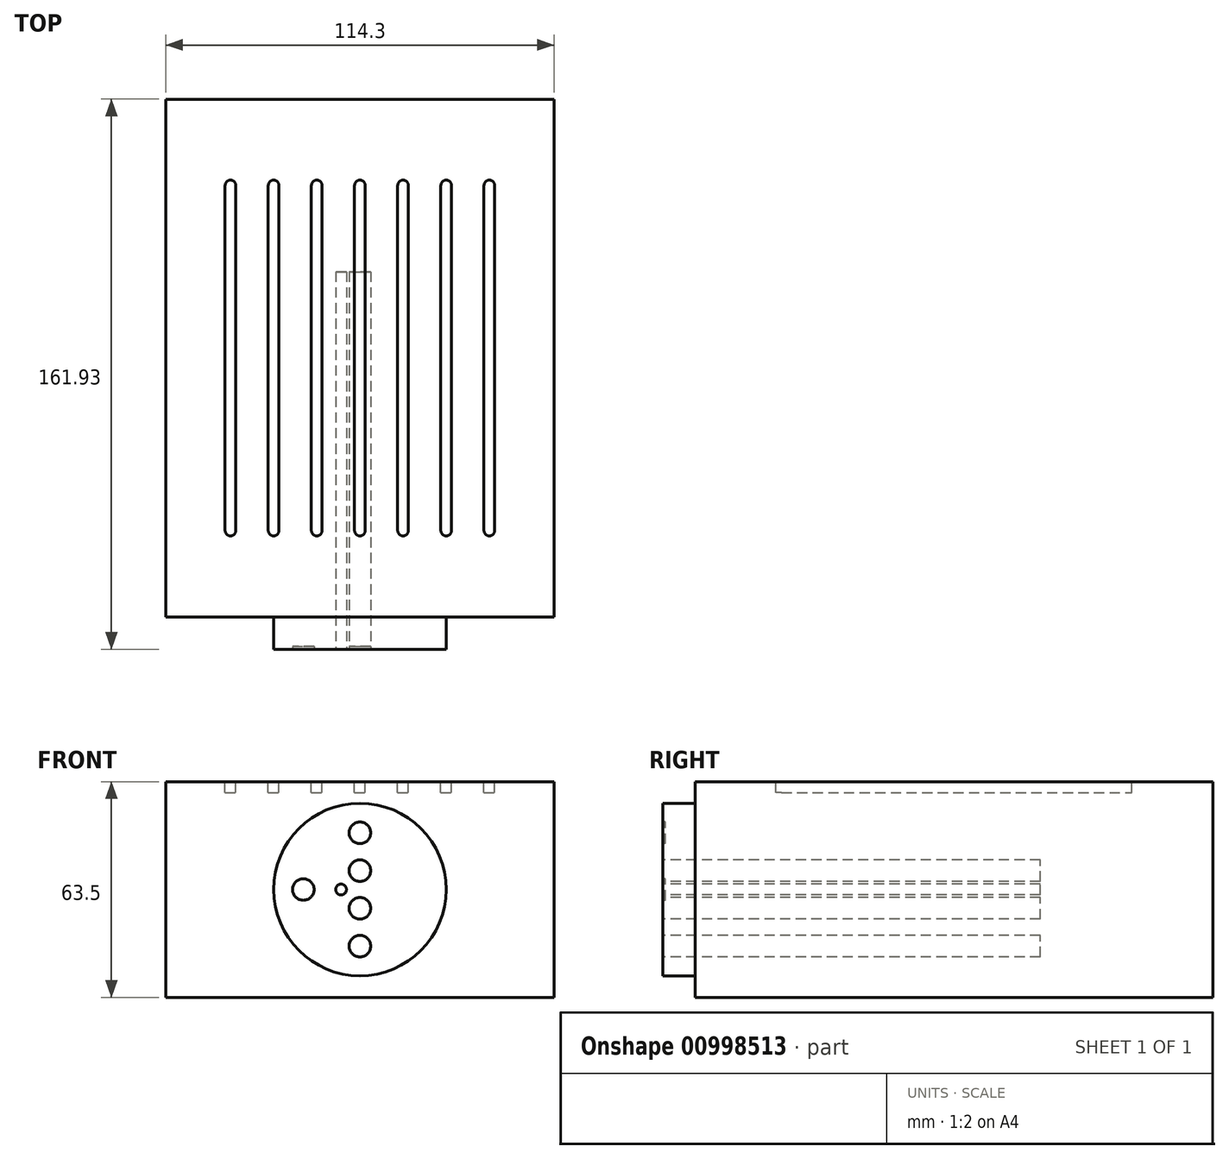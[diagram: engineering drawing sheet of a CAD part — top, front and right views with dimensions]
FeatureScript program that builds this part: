
annotation { "Feature Type Name" : "Feature", "Feature Type Description" : "" }
export const myFeature = defineFeature(function(context is Context, id is Id, definition is map)
    precondition{}
    {
        {
            var Q0;
            Q0=qCreatedBy(makeId("Front.planeOp"),FACE);
            var sketch = newSketch(context, id + "F0", { "sketchPlane" : qUnion([Q0])});
            skCircle(sketch, "E0", {"center": v(0, 0) * mm, "radius": 25.4 * mm});
            skLineSegment(sketch, "E1", {"start": v(0, 0) * mm, "end": v(0, -22.23) * mm, "construction": true});
            skCircle(sketch, "E2", {"center": v(0, -11.11) * mm, "radius": 11.11 * mm, "construction": true});
            skLineSegment(sketch, "E3", {"start": v(0, 0) * mm, "end": v(0, -11.11) * mm, "construction": true});
            skLineSegment(sketch, "E4", {"start": v(0, -11.11) * mm, "end": v(0, -22.23) * mm, "construction": true});
            skCircle(sketch, "E5", {"center": v(0, -5.56) * mm, "radius": 3.18 * mm});
            skCircle(sketch, "E6", {"center": v(0, -16.67) * mm, "radius": 3.18 * mm});
            skCircle(sketch, "E7.1.0", {"center": v(0, 5.56) * mm, "radius": 3.18 * mm});
            skCircle(sketch, "E7.1.1", {"center": v(0, 16.67) * mm, "radius": 3.18 * mm});
            skCircle(sketch, "E8", {"center": v(-16.67, 0) * mm, "radius": 3.18 * mm});
            skCircle(sketch, "E9", {"center": v(-5.56, 0) * mm, "radius": 1.59 * mm});
            skSolve(sketch);
        }
        {
            var Q0;
            Q0=makeQuery(id+"F0.imprint","IMPRINT",FACE,{"disambiguationData":[TD([[makeQuery(id+"F0.imprint","IMPRINT",EDGE,{"derivedFrom":sQuery(id+"F0.wireOp",EDGE,"E0")}),1.0]])]});
            var Q1;
            Q1=makeQuery(id+"F0.imprint","IMPRINT",FACE,{"disambiguationData":[TD([[makeQuery(id+"F0.imprint","IMPRINT",EDGE,{"derivedFrom":sQuery(id+"F0.wireOp",EDGE,"E8")}),1.0]])]});
            var Q2;
            Q2=makeQuery(id+"F0.imprint","IMPRINT",FACE,{"disambiguationData":[TD([[makeQuery(id+"F0.imprint","IMPRINT",EDGE,{"derivedFrom":sQuery(id+"F0.wireOp",EDGE,"E7.1.1")}),1.0]])]});
            extrude(context, id + "F1", {"entities" : qUnion([Q0, Q1, Q2]), "oppositeDirection" : true, "depth" : 9.52 * mm, "offsetDistance" : 25.4 * mm});
        }
        {
            var Q0;
            Q0=makeQuery(id+"F1.opExtrude","CAP_FACE",FACE,{"disambiguationData":[OSD([sQuery(id+"F0.wireOp",EDGE,"bLrKrRyo-NOmt-zjUR-0U13-k7j1eWPFAlHC"),sQuery(id+"F0.wireOp",EDGE,"oxDvdeo9-2tOV-YATh-vV8f-WV8PJaf9Di6w"),sQuery(id+"F0.wireOp",EDGE,"E0")])],"isStart":false});
            var sketch = newSketch(context, id + "F2", { "sketchPlane" : qUnion([Q0])});
            skLineSegment(sketch, "E10.bottom", {"start": v(57.15, 31.75) * mm, "end": v(-57.15, 31.75) * mm});
            skLineSegment(sketch, "E10.top", {"start": v(57.15, -31.75) * mm, "end": v(-57.15, -31.75) * mm});
            skLineSegment(sketch, "E10.left", {"start": v(57.15, 31.75) * mm, "end": v(57.15, -31.75) * mm});
            skLineSegment(sketch, "E10.right", {"start": v(-57.15, 31.75) * mm, "end": v(-57.15, -31.75) * mm});
            skPoint(sketch, "E10.middle", {"position": v(0, 0) * mm});
            skSolve(sketch);
        }
        {
            var Q0;
            Q0 = qSketchRegion(id + "F2", true);
            extrude(context, id + "F3", {"entities" : qUnion([Q0]), "operationType" : NewBodyOperationType.ADD, "depth" : 152.4 * mm, "offsetDistance" : 25.4 * mm});
        }
        {
            var Q0;
            Q0=makeQuery(id+"F3.opExtrude","SWEPT_FACE",FACE,{"disambiguationData":[OSD([sQuery(id+"F2.wireOp",EDGE,"E10.bottom")])]});
            var sketch = newSketch(context, id + "F4", { "sketchPlane" : qUnion([Q0])});
            skLineSegment(sketch, "E11", {"start": v(0, 34.93) * mm, "end": v(0, 136.53) * mm, "construction": true});
            skPoint(sketch, "E11.startSnap0", {"position": v(0, 9.53) * mm});
            skPoint(sketch, "E11.endSnap0", {"position": v(0, 161.93) * mm});
            skArc(sketch, "E12.0.startCap", {"start": v(1.59, 34.93) * mm, "mid": v(0, 33.34) * mm, "end": v(-1.59, 34.93) * mm});
            skArc(sketch, "E12.0.endCap", {"start": v(-1.59, 136.53) * mm, "mid": v(0, 138.11) * mm, "end": v(1.59, 136.53) * mm});
            skLineSegment(sketch, "E12.0.left", {"start": v(-1.59, 34.93) * mm, "end": v(-1.59, 136.53) * mm});
            skLineSegment(sketch, "E12.0.right", {"start": v(1.59, 34.93) * mm, "end": v(1.59, 136.53) * mm});
            skLineSegment(sketch, "E13.1.0.0", {"start": v(11.11, 34.93) * mm, "end": v(11.11, 136.53) * mm});
            skLineSegment(sketch, "E13.1.0.1", {"start": v(14.29, 34.93) * mm, "end": v(14.29, 136.53) * mm});
            skLineSegment(sketch, "E13.1.0.2", {"start": v(12.7, 34.93) * mm, "end": v(12.7, 136.53) * mm, "construction": true});
            skArc(sketch, "E13.1.0.3", {"start": v(14.29, 34.93) * mm, "mid": v(12.7, 33.34) * mm, "end": v(11.11, 34.93) * mm});
            skArc(sketch, "E13.1.0.4", {"start": v(11.11, 136.53) * mm, "mid": v(12.7, 138.11) * mm, "end": v(14.29, 136.53) * mm});
            skLineSegment(sketch, "E13.2.0.0", {"start": v(23.81, 34.93) * mm, "end": v(23.81, 136.53) * mm});
            skLineSegment(sketch, "E13.2.0.1", {"start": v(26.99, 34.93) * mm, "end": v(26.99, 136.53) * mm});
            skLineSegment(sketch, "E13.2.0.2", {"start": v(25.4, 34.93) * mm, "end": v(25.4, 136.53) * mm, "construction": true});
            skArc(sketch, "E13.2.0.3", {"start": v(26.99, 34.93) * mm, "mid": v(25.4, 33.34) * mm, "end": v(23.81, 34.93) * mm});
            skArc(sketch, "E13.2.0.4", {"start": v(23.81, 136.53) * mm, "mid": v(25.4, 138.11) * mm, "end": v(26.99, 136.53) * mm});
            skLineSegment(sketch, "E13.3.0.0", {"start": v(36.51, 34.93) * mm, "end": v(36.51, 136.53) * mm});
            skLineSegment(sketch, "E13.3.0.1", {"start": v(39.69, 34.93) * mm, "end": v(39.69, 136.53) * mm});
            skLineSegment(sketch, "E13.3.0.2", {"start": v(38.1, 34.93) * mm, "end": v(38.1, 136.53) * mm, "construction": true});
            skArc(sketch, "E13.3.0.3", {"start": v(39.69, 34.93) * mm, "mid": v(38.1, 33.34) * mm, "end": v(36.51, 34.93) * mm});
            skArc(sketch, "E13.3.0.4", {"start": v(36.51, 136.53) * mm, "mid": v(38.1, 138.11) * mm, "end": v(39.69, 136.53) * mm});
            skLineSegment(sketch, "E13.direction1", {"start": v(-1.59, 34.93) * mm, "end": v(11.11, 34.93) * mm, "construction": true});
            skArc(sketch, "E14.MirrorCS", {"start": v(-23.81, 136.53) * mm, "mid": v(-25.4, 138.11) * mm, "end": v(-26.99, 136.53) * mm});
            skArc(sketch, "E15.MirrorCS", {"start": v(-26.99, 34.93) * mm, "mid": v(-25.4, 33.34) * mm, "end": v(-23.81, 34.93) * mm});
            skArc(sketch, "E16.MirrorCS", {"start": v(-11.11, 136.53) * mm, "mid": v(-12.7, 138.11) * mm, "end": v(-14.29, 136.53) * mm});
            skArc(sketch, "E17.MirrorCS", {"start": v(-14.29, 34.93) * mm, "mid": v(-12.7, 33.34) * mm, "end": v(-11.11, 34.93) * mm});
            skArc(sketch, "E18.MirrorCS", {"start": v(-39.69, 34.93) * mm, "mid": v(-38.1, 33.34) * mm, "end": v(-36.51, 34.93) * mm});
            skArc(sketch, "E19.MirrorCS", {"start": v(-36.51, 136.53) * mm, "mid": v(-38.1, 138.11) * mm, "end": v(-39.69, 136.53) * mm});
            skLineSegment(sketch, "E20.MirrorCS", {"start": v(-38.1, 34.93) * mm, "end": v(-38.1, 136.53) * mm, "construction": true});
            skLineSegment(sketch, "E21.MirrorCS", {"start": v(-14.29, 34.93) * mm, "end": v(-14.29, 136.53) * mm});
            skLineSegment(sketch, "E22.MirrorCS", {"start": v(-11.11, 34.93) * mm, "end": v(-11.11, 136.53) * mm});
            skLineSegment(sketch, "E23.MirrorCS", {"start": v(-25.4, 34.93) * mm, "end": v(-25.4, 136.53) * mm, "construction": true});
            skLineSegment(sketch, "E24.MirrorCS", {"start": v(-26.99, 34.93) * mm, "end": v(-26.99, 136.53) * mm});
            skLineSegment(sketch, "E25.MirrorCS", {"start": v(-23.81, 34.93) * mm, "end": v(-23.81, 136.53) * mm});
            skLineSegment(sketch, "E26.MirrorCS", {"start": v(-39.69, 34.93) * mm, "end": v(-39.69, 136.53) * mm});
            skLineSegment(sketch, "E27.MirrorCS", {"start": v(-12.7, 34.93) * mm, "end": v(-12.7, 136.53) * mm, "construction": true});
            skLineSegment(sketch, "E28.MirrorCS", {"start": v(-36.51, 34.93) * mm, "end": v(-36.51, 136.53) * mm});
            skSolve(sketch);
        }
        {
            var Q0;
            Q0 = qSketchRegion(id + "F4", true);
            extrude(context, id + "F5", {"entities" : qUnion([Q0]), "operationType" : NewBodyOperationType.REMOVE, "oppositeDirection" : true, "depth" : 3.17 * mm, "offsetDistance" : 25.4 * mm});
        }
        {
            var Q0;
            Q0=makeQuery(id+"F0.imprint","IMPRINT",FACE,{"disambiguationData":[TD([[makeQuery(id+"F0.imprint","IMPRINT",EDGE,{"derivedFrom":sQuery(id+"F0.wireOp",EDGE,"E7.1.1")}),1.0]])]});
            var Q1;
            Q1=makeQuery(id+"F0.imprint","IMPRINT",FACE,{"disambiguationData":[TD([[makeQuery(id+"F0.imprint","IMPRINT",EDGE,{"derivedFrom":sQuery(id+"F0.wireOp",EDGE,"E8")}),1.0]])]});
            extrude(context, id + "F6", {"entities" : qUnion([Q0, Q1]), "operationType" : NewBodyOperationType.REMOVE, "oppositeDirection" : true, "depth" : 0.8 * mm, "offsetDistance" : 25.4 * mm});
        }
        {
            var Q0;
            Q0=makeQuery(id+"F3.boolean.opBoolean","SPLIT",FACE,{"disambiguationData":[TD([makeQuery(id+"F1.opExtrude","SWEPT_FACE",FACE,{"disambiguationData":[OSD([sQuery(id+"F0.wireOp",EDGE,"E7.1.0")])]})])],"derivedFrom":makeQuery(id+"F3.opExtrude","CAP_FACE",FACE,{"disambiguationData":[OSD([sQuery(id+"F2.wireOp",EDGE,"E10.bottom"),sQuery(id+"F2.wireOp",EDGE,"E10.top"),sQuery(id+"F2.wireOp",EDGE,"E10.left"),sQuery(id+"F2.wireOp",EDGE,"E10.right")])],"isStart":true})});
            var Q1;
            Q1=makeQuery(id+"F3.boolean.opBoolean","SPLIT",FACE,{"disambiguationData":[TD([makeQuery(id+"F1.opExtrude","SWEPT_FACE",FACE,{"disambiguationData":[OSD([sQuery(id+"F0.wireOp",EDGE,"E9")])]})])],"derivedFrom":makeQuery(id+"F3.opExtrude","CAP_FACE",FACE,{"disambiguationData":[OSD([sQuery(id+"F2.wireOp",EDGE,"E10.bottom"),sQuery(id+"F2.wireOp",EDGE,"E10.top"),sQuery(id+"F2.wireOp",EDGE,"E10.left"),sQuery(id+"F2.wireOp",EDGE,"E10.right")])],"isStart":true})});
            var Q2;
            Q2=makeQuery(id+"F3.boolean.opBoolean","SPLIT",FACE,{"disambiguationData":[TD([makeQuery(id+"F1.opExtrude","SWEPT_FACE",FACE,{"disambiguationData":[OSD([sQuery(id+"F0.wireOp",EDGE,"E5")])]})])],"derivedFrom":makeQuery(id+"F3.opExtrude","CAP_FACE",FACE,{"disambiguationData":[OSD([sQuery(id+"F2.wireOp",EDGE,"E10.bottom"),sQuery(id+"F2.wireOp",EDGE,"E10.top"),sQuery(id+"F2.wireOp",EDGE,"E10.left"),sQuery(id+"F2.wireOp",EDGE,"E10.right")])],"isStart":true})});
            var Q3;
            Q3=makeQuery(id+"F3.boolean.opBoolean","SPLIT",FACE,{"disambiguationData":[TD([makeQuery(id+"F1.opExtrude","SWEPT_FACE",FACE,{"disambiguationData":[OSD([sQuery(id+"F0.wireOp",EDGE,"E6")])]})])],"derivedFrom":makeQuery(id+"F3.opExtrude","CAP_FACE",FACE,{"disambiguationData":[OSD([sQuery(id+"F2.wireOp",EDGE,"E10.bottom"),sQuery(id+"F2.wireOp",EDGE,"E10.top"),sQuery(id+"F2.wireOp",EDGE,"E10.left"),sQuery(id+"F2.wireOp",EDGE,"E10.right")])],"isStart":true})});
            extrude(context, id + "F7", {"entities" : qUnion([Q0, Q1, Q2, Q3]), "operationType" : NewBodyOperationType.REMOVE, "oppositeDirection" : true, "depth" : 101.6 * mm, "offsetDistance" : 25.4 * mm});
        }
    });
